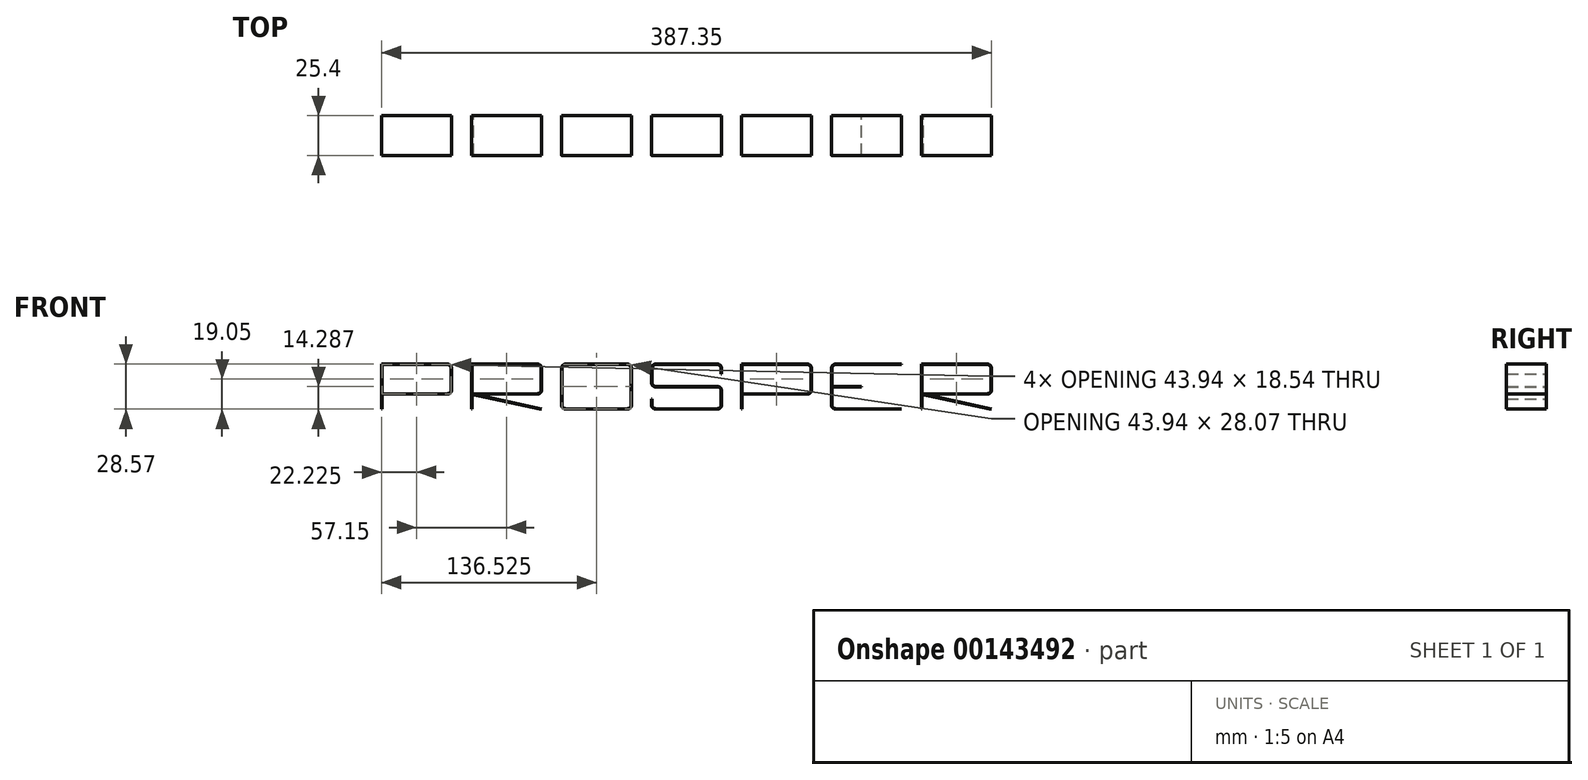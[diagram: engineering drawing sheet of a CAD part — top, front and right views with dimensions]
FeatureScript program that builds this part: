
annotation { "Feature Type Name" : "Feature", "Feature Type Description" : "" }
export const myFeature = defineFeature(function(context is Context, id is Id, definition is map)
    precondition{}
    {
        {
            var Q0;
            Q0=qCreatedBy(makeId("Front.planeOp"),FACE);
            var sketch = newSketch(context, id + "F0", { "sketchPlane" : qUnion([Q0])});
            skLineSegment(sketch, "E0", {"start": v(50.8, 0) * mm, "end": v(50.8, 28.57) * mm});
            skLineSegment(sketch, "E1", {"start": v(50.8, 28.57) * mm, "end": v(95.25, 28.57) * mm});
            skLineSegment(sketch, "E2", {"start": v(95.25, 28.57) * mm, "end": v(95.25, 9.52) * mm});
            skLineSegment(sketch, "E3", {"start": v(95.25, 9.52) * mm, "end": v(50.8, 9.52) * mm});
            skLineSegment(sketch, "E4", {"start": v(107.95, 0) * mm, "end": v(107.95, 28.57) * mm});
            skLineSegment(sketch, "E5", {"start": v(107.95, 28.57) * mm, "end": v(152.4, 28.57) * mm});
            skLineSegment(sketch, "E6", {"start": v(152.4, 28.57) * mm, "end": v(152.4, 9.52) * mm});
            skLineSegment(sketch, "E7", {"start": v(152.4, 9.52) * mm, "end": v(107.95, 9.52) * mm});
            skLineSegment(sketch, "E8", {"start": v(109.13, 9.52) * mm, "end": v(152.4, 0) * mm});
            skLineSegment(sketch, "E9", {"start": v(165.1, 0) * mm, "end": v(165.1, 28.57) * mm});
            skLineSegment(sketch, "E10", {"start": v(165.1, 28.57) * mm, "end": v(209.55, 28.57) * mm});
            skLineSegment(sketch, "E11", {"start": v(209.55, 28.57) * mm, "end": v(209.55, 0) * mm});
            skLineSegment(sketch, "E12", {"start": v(209.55, 0) * mm, "end": v(165.1, 0) * mm});
            skLineSegment(sketch, "E13", {"start": v(222.25, 6.35) * mm, "end": v(222.25, 0) * mm});
            skLineSegment(sketch, "E14", {"start": v(222.25, 0) * mm, "end": v(266.7, 0) * mm});
            skLineSegment(sketch, "E15", {"start": v(266.7, 0) * mm, "end": v(266.7, 14.41) * mm});
            skLineSegment(sketch, "E16", {"start": v(266.7, 14.29) * mm, "end": v(222.25, 14.29) * mm});
            skLineSegment(sketch, "E17", {"start": v(222.25, 14.16) * mm, "end": v(222.25, 28.57) * mm});
            skLineSegment(sketch, "E18", {"start": v(222.25, 28.57) * mm, "end": v(266.7, 28.57) * mm});
            skLineSegment(sketch, "E19", {"start": v(266.7, 28.57) * mm, "end": v(266.7, 22.22) * mm});
            skLineSegment(sketch, "E20", {"start": v(279.4, 0) * mm, "end": v(279.4, 28.57) * mm});
            skLineSegment(sketch, "E21", {"start": v(279.4, 28.57) * mm, "end": v(323.85, 28.57) * mm});
            skLineSegment(sketch, "E22", {"start": v(323.85, 28.57) * mm, "end": v(323.85, 9.53) * mm});
            skLineSegment(sketch, "E23", {"start": v(323.85, 9.53) * mm, "end": v(279.4, 9.53) * mm});
            skLineSegment(sketch, "E24", {"start": v(336.55, 28.58) * mm, "end": v(336.55, 0) * mm});
            skLineSegment(sketch, "E25", {"start": v(336.55, 28.58) * mm, "end": v(381, 28.58) * mm});
            skLineSegment(sketch, "E26", {"start": v(393.7, 0) * mm, "end": v(393.7, 28.57) * mm});
            skLineSegment(sketch, "E27", {"start": v(393.7, 28.57) * mm, "end": v(438.15, 28.57) * mm});
            skLineSegment(sketch, "E28", {"start": v(438.15, 28.57) * mm, "end": v(438.15, 9.52) * mm});
            skLineSegment(sketch, "E29", {"start": v(438.15, 9.52) * mm, "end": v(393.7, 9.52) * mm});
            skLineSegment(sketch, "E30", {"start": v(394.88, 9.53) * mm, "end": v(438.15, 0) * mm});
            skLineSegment(sketch, "E31", {"start": v(336.55, 0) * mm, "end": v(381, 0) * mm});
            skLineSegment(sketch, "E32", {"start": v(336.55, 14.29) * mm, "end": v(355.6, 14.29) * mm});
            skLineSegment(sketch, "E33.0", {"start": v(51.05, 28.32) * mm, "end": v(95, 28.32) * mm});
            skLineSegment(sketch, "E34.0", {"start": v(95, 9.78) * mm, "end": v(50.8, 9.78) * mm});
            skLineSegment(sketch, "E34.1", {"start": v(95, 28.32) * mm, "end": v(95, 9.78) * mm});
            skLineSegment(sketch, "E35.0", {"start": v(51.05, 0) * mm, "end": v(51.05, 28.32) * mm});
            skLineSegment(sketch, "E36.0", {"start": v(152.15, 28.32) * mm, "end": v(152.15, 9.78) * mm});
            skLineSegment(sketch, "E36.1", {"start": v(108.2, 28.32) * mm, "end": v(152.15, 28.32) * mm});
            skLineSegment(sketch, "E37.0", {"start": v(108.2, 0) * mm, "end": v(108.2, 28.32) * mm});
            skLineSegment(sketch, "E38.0", {"start": v(152.15, 9.78) * mm, "end": v(107.95, 9.78) * mm});
            skLineSegment(sketch, "E39.0", {"start": v(107.95, 9.53) * mm, "end": v(151.22, 0) * mm});
            skLineSegment(sketch, "E40", {"start": v(108.2, 0) * mm, "end": v(107.95, 0) * mm});
            skLineSegment(sketch, "E41", {"start": v(151.22, 0) * mm, "end": v(152.4, 0) * mm});
            skPoint(sketch, "E42.orphan", {"position": v(152.4, 0) * mm});
            skLineSegment(sketch, "E43", {"start": v(50.8, 0) * mm, "end": v(51.05, 0) * mm});
            skLineSegment(sketch, "E44.0", {"start": v(165.35, 28.32) * mm, "end": v(209.3, 28.32) * mm});
            skLineSegment(sketch, "E44.1", {"start": v(165.35, 0.25) * mm, "end": v(165.35, 28.32) * mm});
            skLineSegment(sketch, "E44.2", {"start": v(209.3, 0.25) * mm, "end": v(165.35, 0.25) * mm});
            skLineSegment(sketch, "E44.3", {"start": v(209.3, 28.32) * mm, "end": v(209.3, 0.25) * mm});
            skLineSegment(sketch, "E45.0", {"start": v(222.5, 6.35) * mm, "end": v(222.5, 0.25) * mm});
            skLineSegment(sketch, "E46.0", {"start": v(266.45, 0.25) * mm, "end": v(266.45, 14.16) * mm});
            skLineSegment(sketch, "E46.1", {"start": v(222.5, 0.25) * mm, "end": v(266.45, 0.25) * mm});
            skLineSegment(sketch, "E47.0", {"start": v(266.45, 28.32) * mm, "end": v(266.45, 22.22) * mm});
            skLineSegment(sketch, "E48.0", {"start": v(222.5, 28.32) * mm, "end": v(266.45, 28.32) * mm});
            skLineSegment(sketch, "E48.1", {"start": v(222.5, 14.41) * mm, "end": v(222.5, 28.32) * mm});
            skLineSegment(sketch, "E49.0", {"start": v(266.7, 14.41) * mm, "end": v(222.5, 14.41) * mm});
            skLineSegment(sketch, "E50.0", {"start": v(266.45, 14.16) * mm, "end": v(222.25, 14.16) * mm});
            skLineSegment(sketch, "E51", {"start": v(222.25, 6.35) * mm, "end": v(222.5, 6.35) * mm});
            skLineSegment(sketch, "E52", {"start": v(266.45, 22.22) * mm, "end": v(266.7, 22.22) * mm});
            skLineSegment(sketch, "E53.0", {"start": v(323.6, 9.78) * mm, "end": v(279.4, 9.78) * mm});
            skLineSegment(sketch, "E53.1", {"start": v(323.6, 28.32) * mm, "end": v(323.6, 9.78) * mm});
            skLineSegment(sketch, "E53.2", {"start": v(279.65, 28.32) * mm, "end": v(323.6, 28.32) * mm});
            skLineSegment(sketch, "E54.0", {"start": v(279.65, 0) * mm, "end": v(279.65, 28.32) * mm});
            skLineSegment(sketch, "E55", {"start": v(279.65, 0) * mm, "end": v(279.4, 0) * mm});
            skLineSegment(sketch, "E56.0", {"start": v(437.9, 9.78) * mm, "end": v(393.7, 9.78) * mm});
            skLineSegment(sketch, "E56.1", {"start": v(437.9, 28.32) * mm, "end": v(437.9, 9.78) * mm});
            skLineSegment(sketch, "E56.2", {"start": v(393.95, 28.32) * mm, "end": v(437.9, 28.32) * mm});
            skLineSegment(sketch, "E57.0", {"start": v(393.95, 0) * mm, "end": v(393.95, 28.32) * mm});
            skLineSegment(sketch, "E58.0", {"start": v(393.7, 9.52) * mm, "end": v(436.97, 0) * mm});
            skLineSegment(sketch, "E59", {"start": v(393.7, 0) * mm, "end": v(393.95, 0) * mm});
            skLineSegment(sketch, "E60", {"start": v(436.97, 0) * mm, "end": v(438.15, 0) * mm});
            skPoint(sketch, "E61.orphan", {"position": v(438.15, 0) * mm});
            skLineSegment(sketch, "E62.0", {"start": v(336.8, 28.32) * mm, "end": v(381, 28.32) * mm});
            skLineSegment(sketch, "E62.1", {"start": v(336.8, 28.32) * mm, "end": v(336.8, 0.25) * mm});
            skLineSegment(sketch, "E62.2", {"start": v(336.8, 0.25) * mm, "end": v(381, 0.25) * mm});
            skLineSegment(sketch, "E63", {"start": v(381, 28.58) * mm, "end": v(381, 28.32) * mm});
            skLineSegment(sketch, "E64", {"start": v(381, 0.25) * mm, "end": v(381, 0) * mm});
            skLineSegment(sketch, "E65.0", {"start": v(336.55, 14.16) * mm, "end": v(355.6, 14.16) * mm});
            skLineSegment(sketch, "E66.0", {"start": v(336.55, 14.41) * mm, "end": v(355.6, 14.41) * mm});
            skLineSegment(sketch, "E67", {"start": v(355.6, 14.41) * mm, "end": v(355.6, 14.16) * mm});
            skSolve(sketch);
        }
        {
            var Q0;
            Q0 = qSketchRegion(id + "F0", true);
            extrude(context, id + "F1", {"entities" : qUnion([Q0]), "depth" : 25.4 * mm});
        }
        {
            var Q0;
            Q0=makeQuery(id+"F1.opExtrude","SWEPT_EDGE",EDGE,{"disambiguationData":[OSD([sQuery(id+"F0.wireOp",EDGE,"E6"),sQuery(id+"F0.wireOp",EDGE,"E7")])]});
            var Q1;
            Q1=makeQuery(id+"F1.opExtrude","SWEPT_EDGE",EDGE,{"disambiguationData":[OSD([sQuery(id+"F0.wireOp",EDGE,"E39.0"),sQuery(id+"F0.wireOp",EDGE,"E41")])]});
            var Q2;
            Q2=makeQuery(id+"F1.opExtrude","SWEPT_EDGE",EDGE,{"disambiguationData":[OSD([sQuery(id+"F0.wireOp",EDGE,"E33.0"),sQuery(id+"F0.wireOp",EDGE,"E34.1")])]});
            var Q3;
            Q3=makeQuery(id+"F1.opExtrude","SWEPT_EDGE",EDGE,{"disambiguationData":[OSD([sQuery(id+"F0.wireOp",EDGE,"E34.0"),sQuery(id+"F0.wireOp",EDGE,"E34.1")])]});
            var Q4;
            Q4=makeQuery(id+"F1.opExtrude","SWEPT_EDGE",EDGE,{"disambiguationData":[OSD([sQuery(id+"F0.wireOp",EDGE,"E1"),sQuery(id+"F0.wireOp",EDGE,"E2")])]});
            var Q5;
            Q5=makeQuery(id+"F1.opExtrude","SWEPT_EDGE",EDGE,{"disambiguationData":[OSD([sQuery(id+"F0.wireOp",EDGE,"E2"),sQuery(id+"F0.wireOp",EDGE,"E3")])]});
            var Q6;
            Q6=makeQuery(id+"F1.opExtrude","SWEPT_EDGE",EDGE,{"disambiguationData":[OSD([sQuery(id+"F0.wireOp",EDGE,"E6"),sQuery(id+"F0.wireOp",EDGE,"E7")])]});
            var Q7;
            Q7=makeQuery(id+"F1.opExtrude","SWEPT_EDGE",EDGE,{"disambiguationData":[OSD([sQuery(id+"F0.wireOp",EDGE,"E5"),sQuery(id+"F0.wireOp",EDGE,"E6")])]});
            var Q8;
            Q8=makeQuery(id+"F1.opExtrude","SWEPT_EDGE",EDGE,{"disambiguationData":[OSD([sQuery(id+"F0.wireOp",EDGE,"E36.0"),sQuery(id+"F0.wireOp",EDGE,"E36.1")])]});
            var Q9;
            Q9=makeQuery(id+"F1.opExtrude","SWEPT_EDGE",EDGE,{"disambiguationData":[OSD([sQuery(id+"F0.wireOp",EDGE,"E36.0"),sQuery(id+"F0.wireOp",EDGE,"E38.0")])]});
            var Q10;
            Q10=makeQuery(id+"F1.opExtrude","SWEPT_EDGE",EDGE,{"disambiguationData":[OSD([sQuery(id+"F0.wireOp",EDGE,"E44.2"),sQuery(id+"F0.wireOp",EDGE,"E44.3")])]});
            var Q11;
            Q11=makeQuery(id+"F1.opExtrude","SWEPT_EDGE",EDGE,{"disambiguationData":[OSD([sQuery(id+"F0.wireOp",EDGE,"E44.1"),sQuery(id+"F0.wireOp",EDGE,"E44.2")])]});
            var Q12;
            Q12=makeQuery(id+"F1.opExtrude","SWEPT_EDGE",EDGE,{"disambiguationData":[OSD([sQuery(id+"F0.wireOp",EDGE,"E10"),sQuery(id+"F0.wireOp",EDGE,"E11")])]});
            var Q13;
            Q13=makeQuery(id+"F1.opExtrude","SWEPT_EDGE",EDGE,{"disambiguationData":[OSD([sQuery(id+"F0.wireOp",EDGE,"E11"),sQuery(id+"F0.wireOp",EDGE,"E12")])]});
            var Q14;
            Q14=makeQuery(id+"F1.opExtrude","SWEPT_EDGE",EDGE,{"disambiguationData":[OSD([sQuery(id+"F0.wireOp",EDGE,"E9"),sQuery(id+"F0.wireOp",EDGE,"E10")])]});
            var Q15;
            Q15=makeQuery(id+"F1.opExtrude","SWEPT_EDGE",EDGE,{"disambiguationData":[OSD([sQuery(id+"F0.wireOp",EDGE,"E44.0"),sQuery(id+"F0.wireOp",EDGE,"E44.1")])]});
            var Q16;
            Q16=makeQuery(id+"F1.opExtrude","SWEPT_EDGE",EDGE,{"disambiguationData":[OSD([sQuery(id+"F0.wireOp",EDGE,"E9"),sQuery(id+"F0.wireOp",EDGE,"E12")])]});
            var Q17;
            Q17=makeQuery(id+"F1.opExtrude","SWEPT_EDGE",EDGE,{"disambiguationData":[OSD([sQuery(id+"F0.wireOp",EDGE,"E44.0"),sQuery(id+"F0.wireOp",EDGE,"E44.3")])]});
            var Q18;
            Q18=makeQuery(id+"F1.opExtrude","SWEPT_EDGE",EDGE,{"disambiguationData":[OSD([sQuery(id+"F0.wireOp",EDGE,"E45.0"),sQuery(id+"F0.wireOp",EDGE,"E46.1")])]});
            var Q19;
            Q19=makeQuery(id+"F1.opExtrude","SWEPT_EDGE",EDGE,{"disambiguationData":[OSD([sQuery(id+"F0.wireOp",EDGE,"E46.0"),sQuery(id+"F0.wireOp",EDGE,"E50.0")])]});
            var Q20;
            Q20=makeQuery(id+"F1.opExtrude","SWEPT_EDGE",EDGE,{"disambiguationData":[OSD([sQuery(id+"F0.wireOp",EDGE,"E47.0"),sQuery(id+"F0.wireOp",EDGE,"E48.0")])]});
            var Q21;
            Q21=makeQuery(id+"F1.opExtrude","SWEPT_EDGE",EDGE,{"disambiguationData":[OSD([sQuery(id+"F0.wireOp",EDGE,"E46.0"),sQuery(id+"F0.wireOp",EDGE,"E46.1")])]});
            var Q22;
            Q22=makeQuery(id+"F1.opExtrude","SWEPT_EDGE",EDGE,{"disambiguationData":[OSD([sQuery(id+"F0.wireOp",EDGE,"E48.1"),sQuery(id+"F0.wireOp",EDGE,"E49.0")])]});
            var Q23;
            Q23=makeQuery(id+"F1.opExtrude","SWEPT_EDGE",EDGE,{"disambiguationData":[OSD([sQuery(id+"F0.wireOp",EDGE,"E48.0"),sQuery(id+"F0.wireOp",EDGE,"E48.1")])]});
            var Q24;
            Q24=makeQuery(id+"F1.opExtrude","SWEPT_EDGE",EDGE,{"disambiguationData":[OSD([sQuery(id+"F0.wireOp",EDGE,"E17"),sQuery(id+"F0.wireOp",EDGE,"E18")])]});
            var Q25;
            Q25=makeQuery(id+"F1.opExtrude","SWEPT_EDGE",EDGE,{"disambiguationData":[OSD([sQuery(id+"F0.wireOp",EDGE,"E17"),sQuery(id+"F0.wireOp",EDGE,"E50.0")])]});
            var Q26;
            Q26=makeQuery(id+"F1.opExtrude","SWEPT_EDGE",EDGE,{"disambiguationData":[OSD([sQuery(id+"F0.wireOp",EDGE,"E13"),sQuery(id+"F0.wireOp",EDGE,"E14")])]});
            var Q27;
            Q27=makeQuery(id+"F1.opExtrude","SWEPT_EDGE",EDGE,{"disambiguationData":[OSD([sQuery(id+"F0.wireOp",EDGE,"E15"),sQuery(id+"F0.wireOp",EDGE,"E49.0")])]});
            var Q28;
            Q28=makeQuery(id+"F1.opExtrude","SWEPT_EDGE",EDGE,{"disambiguationData":[OSD([sQuery(id+"F0.wireOp",EDGE,"E14"),sQuery(id+"F0.wireOp",EDGE,"E15")])]});
            var Q29;
            Q29=makeQuery(id+"F1.opExtrude","SWEPT_EDGE",EDGE,{"disambiguationData":[OSD([sQuery(id+"F0.wireOp",EDGE,"E18"),sQuery(id+"F0.wireOp",EDGE,"E19")])]});
            var Q30;
            Q30=makeQuery(id+"F1.opExtrude","SWEPT_EDGE",EDGE,{"disambiguationData":[OSD([sQuery(id+"F0.wireOp",EDGE,"E53.0"),sQuery(id+"F0.wireOp",EDGE,"E53.1")])]});
            var Q31;
            Q31=makeQuery(id+"F1.opExtrude","SWEPT_EDGE",EDGE,{"disambiguationData":[OSD([sQuery(id+"F0.wireOp",EDGE,"E53.1"),sQuery(id+"F0.wireOp",EDGE,"E53.2")])]});
            var Q32;
            Q32=makeQuery(id+"F1.opExtrude","SWEPT_EDGE",EDGE,{"disambiguationData":[OSD([sQuery(id+"F0.wireOp",EDGE,"E22"),sQuery(id+"F0.wireOp",EDGE,"E23")])]});
            var Q33;
            Q33=makeQuery(id+"F1.opExtrude","SWEPT_EDGE",EDGE,{"disambiguationData":[OSD([sQuery(id+"F0.wireOp",EDGE,"E21"),sQuery(id+"F0.wireOp",EDGE,"E22")])]});
            var Q34;
            Q34=makeQuery(id+"F1.opExtrude","SWEPT_EDGE",EDGE,{"disambiguationData":[OSD([sQuery(id+"F0.wireOp",EDGE,"E62.1"),sQuery(id+"F0.wireOp",EDGE,"E62.2")])]});
            var Q35;
            Q35=makeQuery(id+"F1.opExtrude","SWEPT_EDGE",EDGE,{"disambiguationData":[OSD([sQuery(id+"F0.wireOp",EDGE,"E24"),sQuery(id+"F0.wireOp",EDGE,"E25")])]});
            var Q36;
            Q36=makeQuery(id+"F1.opExtrude","SWEPT_EDGE",EDGE,{"disambiguationData":[OSD([sQuery(id+"F0.wireOp",EDGE,"E62.0"),sQuery(id+"F0.wireOp",EDGE,"E62.1")])]});
            var Q37;
            Q37=makeQuery(id+"F1.opExtrude","SWEPT_EDGE",EDGE,{"disambiguationData":[OSD([sQuery(id+"F0.wireOp",EDGE,"E24"),sQuery(id+"F0.wireOp",EDGE,"E31")])]});
            var Q38;
            Q38=makeQuery(id+"F1.opExtrude","SWEPT_EDGE",EDGE,{"disambiguationData":[OSD([sQuery(id+"F0.wireOp",EDGE,"E27"),sQuery(id+"F0.wireOp",EDGE,"E28")])]});
            var Q39;
            Q39=makeQuery(id+"F1.opExtrude","SWEPT_EDGE",EDGE,{"disambiguationData":[OSD([sQuery(id+"F0.wireOp",EDGE,"E56.1"),sQuery(id+"F0.wireOp",EDGE,"E56.2")])]});
            var Q40;
            Q40=makeQuery(id+"F1.opExtrude","SWEPT_EDGE",EDGE,{"disambiguationData":[OSD([sQuery(id+"F0.wireOp",EDGE,"E28"),sQuery(id+"F0.wireOp",EDGE,"E29")])]});
            var Q41;
            Q41=makeQuery(id+"F1.opExtrude","SWEPT_EDGE",EDGE,{"disambiguationData":[OSD([sQuery(id+"F0.wireOp",EDGE,"E28"),sQuery(id+"F0.wireOp",EDGE,"E29")])]});
            var Q42;
            Q42=makeQuery(id+"F1.opExtrude","SWEPT_EDGE",EDGE,{"disambiguationData":[OSD([sQuery(id+"F0.wireOp",EDGE,"E58.0"),sQuery(id+"F0.wireOp",EDGE,"E60")])]});
            var Q43;
            Q43=makeQuery(id+"F1.opExtrude","SWEPT_EDGE",EDGE,{"disambiguationData":[OSD([sQuery(id+"F0.wireOp",EDGE,"E56.0"),sQuery(id+"F0.wireOp",EDGE,"E56.1")])]});
            fillet(context, id + "F2", {"entities" : qUnion([Q0, Q1, Q2, Q3, Q4, Q5, Q6, Q7, Q8, Q9, Q10, Q11, Q12, Q13, Q14, Q15, Q16, Q17, Q18, Q19, Q20, Q21, Q22, Q23, Q24, Q25, Q26, Q27, Q28, Q29, Q30, Q31, Q32, Q33, Q34, Q35, Q36, Q37, Q38, Q39, Q40, Q41, Q42, Q43]), "radius" : 2.54 * mm, "tangentPropagation" : true, "allowEdgeOverflow" : false});
        }
    });
